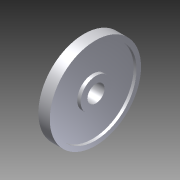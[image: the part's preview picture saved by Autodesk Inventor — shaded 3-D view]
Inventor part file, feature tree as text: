
AUTODESK INVENTOR PART (.ipt)
format: ipt  version: 2012 (Build 160160000, 160)  size: 609,792 bytes
history: native  units: in
note: dims shown in document units (in); Inventor stores cm internally (conversion verified against a paired STEP export)
features: extrude x3, sketch x1, imported_body x1
ambient origin geometry x8: Origin, YZ Plane, XZ Plane, XY Plane, X Axis, Y Axis, Z Axis, Center Point
feature tree (5):
  sketch  "Sketch1"  dims[d0=0.375in d3=0.3in d4=0.0in d5=1.0in d6=0.125in d7=0.125in d8=0.0625in d9=0.5625in d10=0.3in d11=0.0in d12=2.0in d13=1.0in d14=0.0in]
  extrude  "Extrusion2"  Depth=0.3in TaperAngle=0.0deg
  extrude  "Extrusion3"  Depth=1.0in
  extrude  "Extrusion4"  Depth=0.125in
  imported_body  "Base1"
